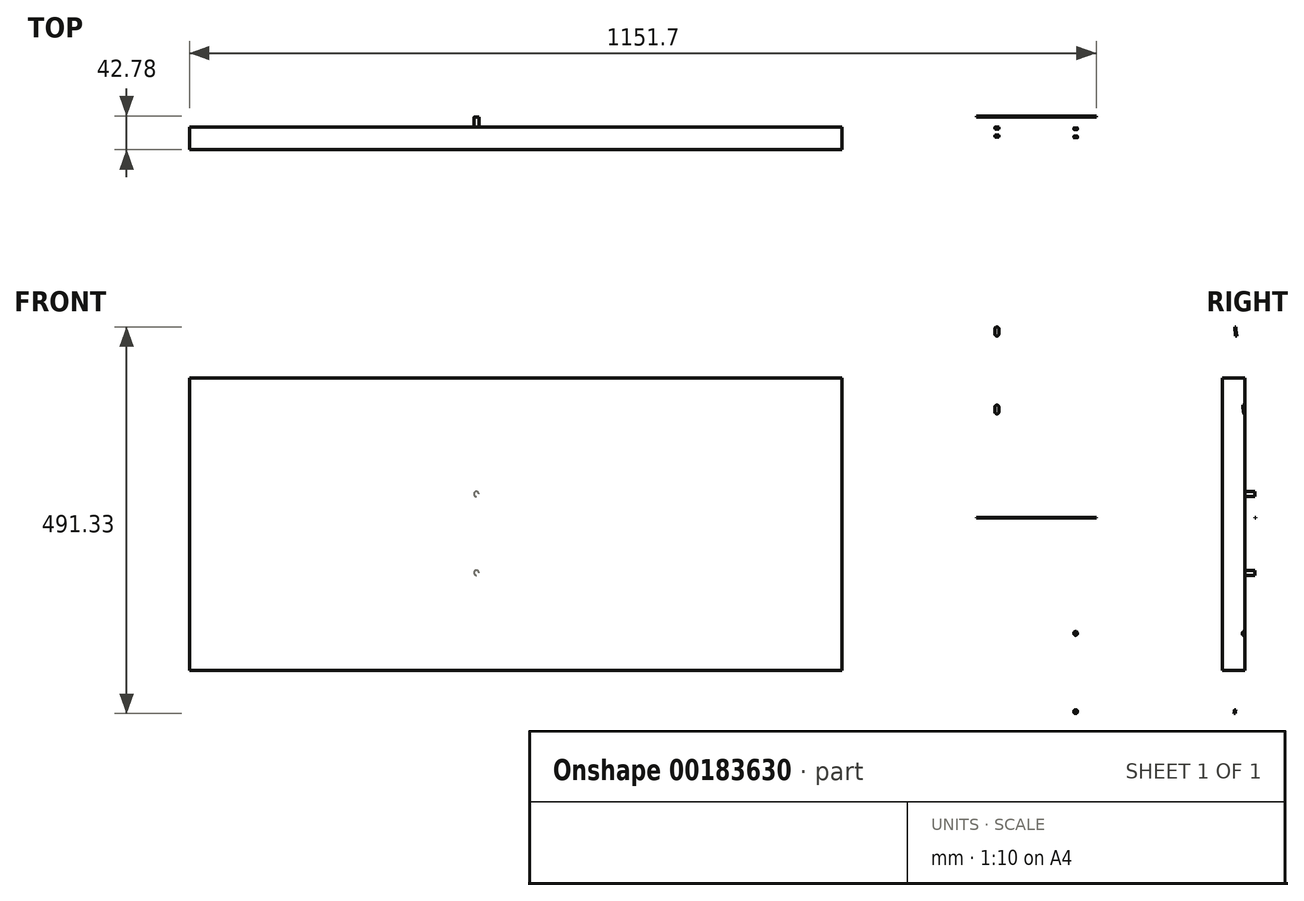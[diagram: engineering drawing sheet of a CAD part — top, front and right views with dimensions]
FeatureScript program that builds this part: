
annotation { "Feature Type Name" : "Feature", "Feature Type Description" : "" }
export const myFeature = defineFeature(function(context is Context, id is Id, definition is map)
    precondition{}
    {
        {
            var Q0;
            Q0=qCreatedBy(makeId("Right.planeOp"),FACE);
            var sketch = newSketch(context, id + "F0", { "sketchPlane" : qUnion([Q0])});
            skLineSegment(sketch, "E0", {"start": v(-0.03, -0.33) * mm, "end": v(-27.88, -265.24) * mm});
            skLineSegment(sketch, "E1", {"start": v(-0.03, 0.33) * mm, "end": v(-27.88, 265.24) * mm});
            skLineSegment(sketch, "E2.0", {"start": v(1.5, 0.33) * mm, "end": v(-26.36, 265.4) * mm});
            skLineSegment(sketch, "E2.1", {"start": v(1.5, -0.33) * mm, "end": v(-26.36, -265.4) * mm});
            skLineSegment(sketch, "E3", {"start": v(-27.88, 265.24) * mm, "end": v(-26.36, 265.4) * mm});
            skLineSegment(sketch, "E4", {"start": v(-27.88, -265.24) * mm, "end": v(-26.36, -265.4) * mm});
            skPoint(sketch, "E5.visualSharp", {"position": v(1.53, 0) * mm});
            skArc(sketch, "E5.filletArc", {"start": v(1.5, -0.33) * mm, "mid": v(1.51, 0) * mm, "end": v(1.5, 0.33) * mm});
            skPoint(sketch, "E6.visualSharp", {"position": v(0, 0) * mm});
            skArc(sketch, "E6.filletArc", {"start": v(-0.03, -0.33) * mm, "mid": v(-0.02, 0) * mm, "end": v(-0.03, 0.33) * mm});
            skSolve(sketch);
        }
        {
            var Q0;
            Q0=makeQuery(id+"F0.imprint","IMPRINT",FACE,{"disambiguationData":[TD([[makeQuery(id+"F0.imprint","IMPRINT",EDGE,{"derivedFrom":sQuery(id+"F0.wireOp",EDGE,"E0")}),1.0]])]});
            extrude(context, id + "F1", {"entities" : qUnion([Q0]), "depth" : 76.2 * mm, "hasSecondDirection" : true, "secondDirectionOppositeDirection" : true, "secondDirectionDepth" : 76.2 * mm});
        }
        {
            var Q0;
            Q0=makeQuery(id+"F1.opExtrude","SWEPT_FACE",FACE,{"disambiguationData":[OSD([sQuery(id+"F0.wireOp",EDGE,"E0")])]});
            var sketch = newSketch(context, id + "F2", { "sketchPlane" : qUnion([Q0])});
            skLineSegment(sketch, "E7", {"start": v(0, 0) * mm, "end": v(0, -266.7) * mm, "construction": true});
            skCircle(sketch, "E8", {"center": v(-50, -247.65) * mm, "radius": 2.38 * mm});
            skCircle(sketch, "E9", {"center": v(-50, -147.65) * mm, "radius": 2.38 * mm});
            skCircle(sketch, "E10.MirrorC", {"center": v(50, -147.65) * mm, "radius": 2.38 * mm});
            skCircle(sketch, "E11.MirrorC", {"center": v(50, -247.65) * mm, "radius": 2.38 * mm});
            skSolve(sketch);
        }
        {
            var Q0;
            Q0=makeQuery(id+"F2.imprint","IMPRINT",FACE,{"disambiguationData":[TD([[makeQuery(id+"F2.imprint","IMPRINT",EDGE,{"derivedFrom":sQuery(id+"F2.wireOp",EDGE,"E9")}),1.0]])]});
            var Q1;
            Q1=makeQuery(id+"F2.imprint","IMPRINT",FACE,{"disambiguationData":[TD([[makeQuery(id+"F2.imprint","IMPRINT",EDGE,{"derivedFrom":sQuery(id+"F2.wireOp",EDGE,"E10.MirrorC")}),-1.0]])]});
            var Q2;
            Q2=makeQuery(id+"F2.imprint","IMPRINT",FACE,{"disambiguationData":[TD([[makeQuery(id+"F2.imprint","IMPRINT",EDGE,{"derivedFrom":sQuery(id+"F2.wireOp",EDGE,"E11.MirrorC")}),-1.0]])]});
            var Q3;
            Q3=makeQuery(id+"F2.imprint","IMPRINT",FACE,{"disambiguationData":[TD([[makeQuery(id+"F2.imprint","IMPRINT",EDGE,{"derivedFrom":sQuery(id+"F2.wireOp",EDGE,"E8")}),1.0]])]});
            extrude(context, id + "F3", {"entities" : qUnion([Q0, Q1, Q2, Q3]), "operationType" : NewBodyOperationType.REMOVE, "endBound" : BoundingType.THROUGH_ALL, "oppositeDirection" : true, "depth" : 25.4 * mm});
        }
        {
            var Q0;
            Q0=makeQuery(id+"F1.opExtrude","SWEPT_FACE",FACE,{"disambiguationData":[OSD([sQuery(id+"F0.wireOp",EDGE,"E1")])]});
            var sketch = newSketch(context, id + "F4", { "sketchPlane" : qUnion([Q0])});
            skLineSegment(sketch, "E12", {"start": v(0, 309.5) * mm, "end": v(0, 120.36) * mm, "construction": true});
            skLineSegment(sketch, "E13", {"start": v(-50, 141.3) * mm, "end": v(-50, 134.95) * mm});
            skLineSegment(sketch, "E14", {"start": v(-50, 241.3) * mm, "end": v(-50, 234.37) * mm});
            skArc(sketch, "E15.0.startCap", {"start": v(-52.38, 241.3) * mm, "mid": v(-50, 243.68) * mm, "end": v(-47.62, 241.3) * mm});
            skArc(sketch, "E15.0.endCap", {"start": v(-47.62, 234.37) * mm, "mid": v(-50, 232) * mm, "end": v(-52.38, 234.37) * mm});
            skLineSegment(sketch, "E15.0.left", {"start": v(-47.62, 241.3) * mm, "end": v(-47.62, 234.37) * mm});
            skLineSegment(sketch, "E15.0.right", {"start": v(-52.38, 241.3) * mm, "end": v(-52.38, 234.37) * mm});
            skArc(sketch, "E15.1.startCap", {"start": v(-52.38, 141.3) * mm, "mid": v(-50, 143.68) * mm, "end": v(-47.62, 141.3) * mm});
            skArc(sketch, "E15.1.endCap", {"start": v(-47.62, 134.95) * mm, "mid": v(-50, 132.57) * mm, "end": v(-52.38, 134.95) * mm});
            skLineSegment(sketch, "E15.1.left", {"start": v(-47.62, 141.3) * mm, "end": v(-47.62, 134.95) * mm});
            skLineSegment(sketch, "E15.1.right", {"start": v(-52.38, 141.3) * mm, "end": v(-52.38, 134.95) * mm});
            skLineSegment(sketch, "E16.MirrorCS", {"start": v(47.62, 241.3) * mm, "end": v(47.62, 234.37) * mm});
            skArc(sketch, "E17.MirrorCS", {"start": v(52.38, 241.3) * mm, "mid": v(50, 243.68) * mm, "end": v(47.62, 241.3) * mm});
            skLineSegment(sketch, "E18.MirrorCS", {"start": v(52.38, 241.3) * mm, "end": v(52.38, 234.37) * mm});
            skArc(sketch, "E19.MirrorCS", {"start": v(47.62, 234.37) * mm, "mid": v(50, 232) * mm, "end": v(52.38, 234.37) * mm});
            skArc(sketch, "E20.MirrorCS", {"start": v(52.38, 141.3) * mm, "mid": v(50, 143.68) * mm, "end": v(47.62, 141.3) * mm});
            skLineSegment(sketch, "E21.MirrorCS", {"start": v(52.38, 141.3) * mm, "end": v(52.38, 134.95) * mm});
            skArc(sketch, "E22.MirrorCS", {"start": v(47.62, 134.95) * mm, "mid": v(50, 132.57) * mm, "end": v(52.38, 134.95) * mm});
            skLineSegment(sketch, "E23.MirrorCS", {"start": v(47.62, 141.3) * mm, "end": v(47.62, 134.95) * mm});
            skLineSegment(sketch, "E24", {"start": v(-50, 234.37) * mm, "end": v(-50, 141.3) * mm, "construction": true});
            skSolve(sketch);
        }
        {
            var Q0;
            Q0=makeQuery(id+"F4.imprint","IMPRINT",FACE,{"disambiguationData":[TD([[makeQuery(id+"F4.imprint","IMPRINT",EDGE,{"derivedFrom":sQuery(id+"F4.wireOp",EDGE,"E15.0.startCap")}),-1.0]])]});
            var Q1;
            Q1=makeQuery(id+"F4.imprint","IMPRINT",FACE,{"disambiguationData":[TD([[makeQuery(id+"F4.imprint","IMPRINT",EDGE,{"derivedFrom":sQuery(id+"F4.wireOp",EDGE,"E16.MirrorCS")}),1.0]])]});
            var Q2;
            Q2=makeQuery(id+"F4.imprint","IMPRINT",FACE,{"disambiguationData":[TD([[makeQuery(id+"F4.imprint","IMPRINT",EDGE,{"derivedFrom":sQuery(id+"F4.wireOp",EDGE,"E20.MirrorCS")}),1.0]])]});
            var Q3;
            Q3=makeQuery(id+"F4.imprint","IMPRINT",FACE,{"disambiguationData":[TD([[makeQuery(id+"F4.imprint","IMPRINT",EDGE,{"derivedFrom":sQuery(id+"F4.wireOp",EDGE,"E15.1.startCap")}),-1.0]])]});
            extrude(context, id + "F5", {"entities" : qUnion([Q0, Q1, Q2, Q3]), "operationType" : NewBodyOperationType.REMOVE, "endBound" : BoundingType.THROUGH_ALL, "oppositeDirection" : true, "depth" : 25.4 * mm});
        }
        {
            var Q0;
            Q0=qCreatedBy(makeId("Front.planeOp"),FACE);
            var sketch = newSketch(context, id + "F6", { "sketchPlane" : qUnion([Q0])});
            skLineSegment(sketch, "E25.bottom", {"start": v(-1075.5, 177.67) * mm, "end": v(-246.83, 177.67) * mm});
            skLineSegment(sketch, "E25.top", {"start": v(-1075.5, -193.8) * mm, "end": v(-246.83, -193.8) * mm});
            skLineSegment(sketch, "E25.left", {"start": v(-1075.5, 177.67) * mm, "end": v(-1075.5, -193.8) * mm});
            skLineSegment(sketch, "E25.right", {"start": v(-246.83, 177.67) * mm, "end": v(-246.83, -193.8) * mm});
            skSolve(sketch);
        }
        {
            var Q0;
            Q0=makeQuery(id+"F6.imprint","IMPRINT",FACE,{"disambiguationData":[TD([[makeQuery(id+"F6.imprint","IMPRINT",EDGE,{"derivedFrom":sQuery(id+"F6.wireOp",EDGE,"E25.bottom")}),-1.0]])]});
            extrude(context, id + "F7", {"entities" : qUnion([Q0]), "depth" : 41.27 * mm});
        }
        {
            var Q0;
            Q0=makeQuery(id+"F7.opExtrude","CAP_FACE",FACE,{"disambiguationData":[OSD([sQuery(id+"F6.wireOp",EDGE,"E25.bottom"),sQuery(id+"F6.wireOp",EDGE,"E25.top"),sQuery(id+"F6.wireOp",EDGE,"E25.left"),sQuery(id+"F6.wireOp",EDGE,"E25.right")])],"isStart":true});
            var sketch = newSketch(context, id + "F8", { "sketchPlane" : qUnion([Q0])});
            skLineSegment(sketch, "E26", {"start": v(661.17, 177.67) * mm, "end": v(661.17, -193.8) * mm, "construction": true});
            skCircle(sketch, "E27", {"center": v(611.17, -69.98) * mm, "radius": 3.18 * mm});
            skCircle(sketch, "E28", {"center": v(611.17, 30.02) * mm, "radius": 3.18 * mm});
            skCircle(sketch, "E29.MirrorC", {"center": v(711.17, 30.02) * mm, "radius": 3.18 * mm});
            skCircle(sketch, "E30.MirrorC", {"center": v(711.17, -69.98) * mm, "radius": 3.18 * mm});
            skSolve(sketch);
        }
        {
            var Q0;
            Q0=makeQuery(id+"F8.imprint","IMPRINT",FACE,{"disambiguationData":[TD([[makeQuery(id+"F8.imprint","IMPRINT",EDGE,{"derivedFrom":sQuery(id+"F8.wireOp",EDGE,"E28")}),1.0]])]});
            var Q1;
            Q1=makeQuery(id+"F8.imprint","IMPRINT",FACE,{"disambiguationData":[TD([[makeQuery(id+"F8.imprint","IMPRINT",EDGE,{"derivedFrom":sQuery(id+"F8.wireOp",EDGE,"E29.MirrorC")}),-1.0]])]});
            var Q2;
            Q2=makeQuery(id+"F8.imprint","IMPRINT",FACE,{"disambiguationData":[TD([[makeQuery(id+"F8.imprint","IMPRINT",EDGE,{"derivedFrom":sQuery(id+"F8.wireOp",EDGE,"E27")}),1.0]])]});
            var Q3;
            Q3=makeQuery(id+"F8.imprint","IMPRINT",FACE,{"disambiguationData":[TD([[makeQuery(id+"F8.imprint","IMPRINT",EDGE,{"derivedFrom":sQuery(id+"F8.wireOp",EDGE,"E30.MirrorC")}),-1.0]])]});
            extrude(context, id + "F9", {"entities" : qUnion([Q0, Q1, Q2, Q3]), "operationType" : NewBodyOperationType.REMOVE, "oppositeDirection" : true, "depth" : 12.7 * mm});
        }
    });
